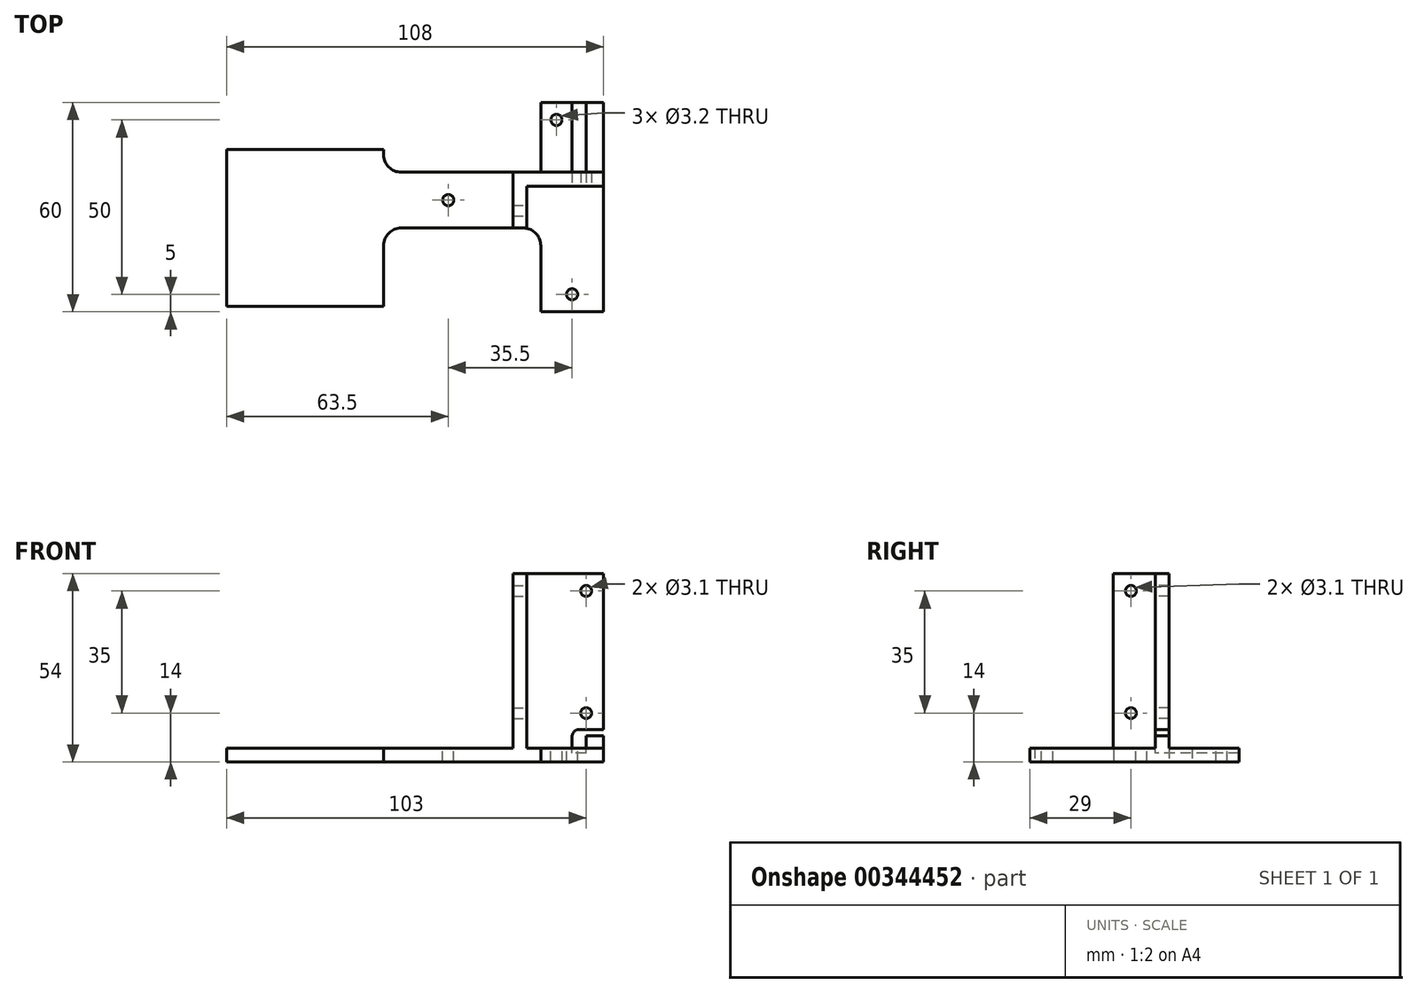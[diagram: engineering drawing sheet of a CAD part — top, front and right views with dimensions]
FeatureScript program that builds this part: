
annotation { "Feature Type Name" : "Feature", "Feature Type Description" : "" }
export const myFeature = defineFeature(function(context is Context, id is Id, definition is map)
    precondition{}
    {
        {
            var Q0;
            Q0=qCreatedBy(makeId("Top.planeOp"),FACE);
            var sketch = newSketch(context, id + "F0", { "sketchPlane" : qUnion([Q0])});
            skLineSegment(sketch, "E0", {"start": v(-54, 26.5) * mm, "end": v(-99, 26.5) * mm});
            skLineSegment(sketch, "E1", {"start": v(-99, 26.5) * mm, "end": v(-99, -18.5) * mm});
            skLineSegment(sketch, "E2", {"start": v(-99, -18.5) * mm, "end": v(-54, -18.5) * mm});
            skLineSegment(sketch, "E3", {"start": v(-54, -18.5) * mm, "end": v(-54, 4) * mm});
            skLineSegment(sketch, "E4", {"start": v(-54, 4) * mm, "end": v(-9, 4) * mm});
            skLineSegment(sketch, "E5", {"start": v(9, 20) * mm, "end": v(-54, 20) * mm});
            skLineSegment(sketch, "E6", {"start": v(-54, 20) * mm, "end": v(-54, 26.5) * mm});
            skLineSegment(sketch, "E7", {"start": v(-9, 4) * mm, "end": v(-9, -20) * mm});
            skLineSegment(sketch, "E8", {"start": v(-9, -20) * mm, "end": v(9, -20) * mm});
            skLineSegment(sketch, "E9", {"start": v(9, -20) * mm, "end": v(9, 20) * mm});
            skPoint(sketch, "E10", {"position": v(0, -20) * mm});
            skPoint(sketch, "E11", {"position": v(9, 0) * mm});
            skSolve(sketch);
        }
        {
            var Q0;
            Q0=makeQuery(id+"F0.imprint","IMPRINT",FACE,{"disambiguationData":[TD([[makeQuery(id+"F0.imprint","IMPRINT",EDGE,{"derivedFrom":sQuery(id+"F0.wireOp",EDGE,"E0")}),1.0]])]});
            extrude(context, id + "F1", {"entities" : qUnion([Q0]), "depth" : 4 * mm});
        }
        {
            var Q0;
            Q0=makeQuery(id+"F1.opExtrude","CAP_FACE",FACE,{"disambiguationData":[OSD([sQuery(id+"F0.wireOp",EDGE,"E0"),sQuery(id+"F0.wireOp",EDGE,"E1"),sQuery(id+"F0.wireOp",EDGE,"E2"),sQuery(id+"F0.wireOp",EDGE,"E3"),sQuery(id+"F0.wireOp",EDGE,"E4"),sQuery(id+"F0.wireOp",EDGE,"E5"),sQuery(id+"F0.wireOp",EDGE,"E6"),sQuery(id+"F0.wireOp",EDGE,"E7"),sQuery(id+"F0.wireOp",EDGE,"E8"),sQuery(id+"F0.wireOp",EDGE,"E9")])],"isStart":false});
            var sketch = newSketch(context, id + "F2", { "sketchPlane" : qUnion([Q0])});
            skLineSegment(sketch, "E12", {"start": v(-17, 4) * mm, "end": v(-17, 20) * mm});
            skPoint(sketch, "E12.endSnap0", {"position": v(-22.5, 20) * mm});
            skLineSegment(sketch, "E13", {"start": v(-17, 20) * mm, "end": v(9, 20) * mm});
            skLineSegment(sketch, "E14", {"start": v(9, 20) * mm, "end": v(9, 16) * mm});
            skLineSegment(sketch, "E15", {"start": v(9, 16) * mm, "end": v(-13, 16) * mm});
            skLineSegment(sketch, "E16", {"start": v(-13, 16) * mm, "end": v(-13, 4) * mm});
            skLineSegment(sketch, "E17", {"start": v(-13, 4) * mm, "end": v(-17, 4) * mm});
            skSolve(sketch);
        }
        {
            var Q0;
            Q0=makeQuery(id+"F2.imprint","IMPRINT",FACE,{"disambiguationData":[TD([[makeQuery(id+"F2.imprint","IMPRINT",EDGE,{"derivedFrom":sQuery(id+"F2.wireOp",EDGE,"E12")}),-1.0]])]});
            var Q1;
            Q1 = qSketchRegion(id + "F2", true);
            extrude(context, id + "F3", {"entities" : qUnion([Q0, Q1]), "operationType" : NewBodyOperationType.ADD, "depth" : 50 * mm});
        }
        {
            var Q0;
            Q0=makeQuery(id+"F3.opExtrude","SWEPT_FACE",FACE,{"disambiguationData":[OSD([sQuery(id+"F2.wireOp",EDGE,"E15")])]});
            var sketch = newSketch(context, id + "F4", { "sketchPlane" : qUnion([Q0])});
            skCircle(sketch, "E18", {"center": v(4, 49) * mm, "radius": 1.55 * mm});
            skCircle(sketch, "E19", {"center": v(4, 14) * mm, "radius": 1.55 * mm});
            skSolve(sketch);
        }
        {
            var Q0;
            Q0 = qSketchRegion(id + "F4", true);
            extrude(context, id + "F5", {"entities" : qUnion([Q0]), "operationType" : NewBodyOperationType.REMOVE, "endBound" : BoundingType.UP_TO_NEXT, "oppositeDirection" : true, "depth" : 25 * mm});
        }
        {
            var Q0;
            Q0=makeQuery(id+"F3.opExtrude","SWEPT_FACE",FACE,{"disambiguationData":[OSD([sQuery(id+"F2.wireOp",EDGE,"E16")])]});
            var sketch = newSketch(context, id + "F6", { "sketchPlane" : qUnion([Q0])});
            skCircle(sketch, "E20", {"center": v(9, 49) * mm, "radius": 1.55 * mm});
            skCircle(sketch, "E21", {"center": v(9, 14) * mm, "radius": 1.55 * mm});
            skSolve(sketch);
        }
        {
            var Q0;
            Q0 = qSketchRegion(id + "F6", true);
            extrude(context, id + "F7", {"entities" : qUnion([Q0]), "operationType" : NewBodyOperationType.REMOVE, "endBound" : BoundingType.UP_TO_NEXT, "oppositeDirection" : true, "depth" : 25 * mm});
        }
        {
            var Q0;
            Q0=makeQuery(id+"F3.opExtrude","SWEPT_FACE",FACE,{"disambiguationData":[OSD([sQuery(id+"F2.wireOp",EDGE,"E15")])]});
            var sketch = newSketch(context, id + "F8", { "sketchPlane" : qUnion([Q0])});
            skLineSegment(sketch, "E22", {"start": v(9, 9.3) * mm, "end": v(2, 9.3) * mm});
            skLineSegment(sketch, "E23", {"start": v(0, 7.3) * mm, "end": v(0, 4) * mm});
            skLineSegment(sketch, "E24", {"start": v(0, 4) * mm, "end": v(4, 4) * mm});
            skLineSegment(sketch, "E25", {"start": v(4, 4) * mm, "end": v(4, 7.5) * mm});
            skLineSegment(sketch, "E26", {"start": v(4, 7.5) * mm, "end": v(9, 7.5) * mm});
            skLineSegment(sketch, "E27", {"start": v(9, 7.5) * mm, "end": v(9, 9.3) * mm});
            skPoint(sketch, "E28.visualSharp", {"position": v(0, 9.3) * mm});
            skArc(sketch, "E28.filletArc", {"start": v(2, 9.3) * mm, "mid": v(0.59, 8.71) * mm, "end": v(0, 7.3) * mm});
            skSolve(sketch);
        }
        {
            var Q0;
            Q0 = qSketchRegion(id + "F8", true);
            extrude(context, id + "F9", {"entities" : qUnion([Q0]), "operationType" : NewBodyOperationType.REMOVE, "endBound" : BoundingType.UP_TO_NEXT, "oppositeDirection" : true, "depth" : 25 * mm});
        }
        {
            var Q0;
            Q0=makeQuery(id+"F3.boolean.opBoolean","MERGE",FACE,{"derivedFrom":[makeQuery(id+"F1.opExtrude","SWEPT_FACE",FACE,{"disambiguationData":[OSD([sQuery(id+"F0.wireOp",EDGE,"E5")])]}),makeQuery(id+"F3.opExtrude","SWEPT_FACE",FACE,{"disambiguationData":[OSD([sQuery(id+"F2.wireOp",EDGE,"E13")])]})]});
            var sketch = newSketch(context, id + "F10", { "sketchPlane" : qUnion([Q0])});
            skLineSegment(sketch, "E29.bottom", {"start": v(-9, 0) * mm, "end": v(9, 0) * mm});
            skLineSegment(sketch, "E29.top", {"start": v(-9, 4) * mm, "end": v(9, 4) * mm});
            skLineSegment(sketch, "E29.left", {"start": v(-9, 0) * mm, "end": v(-9, 4) * mm});
            skLineSegment(sketch, "E29.right", {"start": v(9, 0) * mm, "end": v(9, 4) * mm});
            skLineSegment(sketch, "E30.0.1", {"start": v(9, 0) * mm, "end": v(9, 4) * mm, "construction": true});
            skLineSegment(sketch, "E30.0.3", {"start": v(9, 4) * mm, "end": v(9, 0) * mm, "construction": true});
            skSolve(sketch);
        }
        {
            var Q0;
            Q0=makeQuery(id+"F10.imprint","IMPRINT",FACE,{"disambiguationData":[TD([[makeQuery(id+"F10.imprint","IMPRINT",EDGE,{"derivedFrom":sQuery(id+"F10.wireOp",EDGE,"E29.bottom")}),1.0]])]});
            extrude(context, id + "F11", {"entities" : qUnion([Q0]), "operationType" : NewBodyOperationType.ADD, "depth" : 20 * mm});
        }
        {
            var Q0;
            {var subQ0=sQuery(id+"F0.wireOp",EDGE,"E8");var subQ1=sQuery(id+"F0.wireOp",EDGE,"E7");var subQ2=sQuery(id+"F0.wireOp",EDGE,"E9");var subQ3=sQuery(id+"F0.wireOp",EDGE,"E4");Q0=makeQuery(id+"F11.boolean.opBoolean","MERGE",FACE,{"derivedFrom":[makeQuery(id+"F9.boolean.opBoolean","MERGE",FACE,{"derivedFrom":[makeQuery(id+"F3.boolean.opBoolean","SPLIT",FACE,{"disambiguationData":[TD([makeQuery(id+"F1.opExtrude","SWEPT_FACE",FACE,{"disambiguationData":[OSD([subQ1])]})])],"derivedFrom":makeQuery(id+"F1.opExtrude","CAP_FACE",FACE,{"disambiguationData":[OSD([sQuery(id+"F0.wireOp",EDGE,"E0"),sQuery(id+"F0.wireOp",EDGE,"E1"),sQuery(id+"F0.wireOp",EDGE,"E2"),sQuery(id+"F0.wireOp",EDGE,"E3"),subQ3,sQuery(id+"F0.wireOp",EDGE,"E5"),sQuery(id+"F0.wireOp",EDGE,"E6"),subQ1,subQ0,subQ2])],"isStart":false})}),makeQuery(id+"F9.opExtrude","SWEPT_FACE",FACE,{"disambiguationData":[OSD([sQuery(id+"F8.wireOp",EDGE,"E24")])]})]}),makeQuery(id+"F11.opExtrude","SWEPT_FACE",FACE,{"disambiguationData":[OSD([sQuery(id+"F10.wireOp",EDGE,"E29.top")])]})]});}
            var sketch = newSketch(context, id + "F12", { "sketchPlane" : qUnion([Q0])});
            skLineSegment(sketch, "E31.bottom", {"start": v(4, 16) * mm, "end": v(0, 16) * mm});
            skLineSegment(sketch, "E31.top", {"start": v(4, 40) * mm, "end": v(0, 40) * mm});
            skLineSegment(sketch, "E31.left", {"start": v(4, 16) * mm, "end": v(4, 40) * mm});
            skLineSegment(sketch, "E31.right", {"start": v(0, 16) * mm, "end": v(0, 40) * mm});
            skSolve(sketch);
        }
        {
            var Q0;
            {var subQ8=sQuery(id+"F12.wireOp",EDGE,"E31.bottom");Q0=makeQuery(id+"F12.imprint","IMPRINT",FACE,{"disambiguationData":[TD([[makeQuery(id+"F12.imprint","IMPRINT",EDGE,{"derivedFrom":subQ8}),-1.0]])]});}
            extrude(context, id + "F13", {"entities" : qUnion([Q0]), "operationType" : NewBodyOperationType.REMOVE, "oppositeDirection" : true, "depth" : 1.5 * mm});
        }
        {
            var Q0;
            {var subQ0=makeQuery(id+"F3.opExtrude","SWEPT_FACE",FACE,{"disambiguationData":[OSD([sQuery(id+"F2.wireOp",EDGE,"E15")])]});var subQ1=sQuery(id+"F0.wireOp",EDGE,"E7");var subQ2=makeQuery(id+"F1.opExtrude","SWEPT_FACE",FACE,{"disambiguationData":[OSD([subQ1])]});var subQ3=makeQuery(id+"F3.opExtrude","SWEPT_FACE",FACE,{"disambiguationData":[OSD([sQuery(id+"F2.wireOp",EDGE,"E17")])]});var subQ4=sQuery(id+"F0.wireOp",EDGE,"E9");var subQ5=makeQuery(id+"F1.opExtrude","SWEPT_FACE",FACE,{"disambiguationData":[OSD([subQ4])]});var subQ6=makeQuery(id+"F3.opExtrude","SWEPT_FACE",FACE,{"disambiguationData":[OSD([sQuery(id+"F2.wireOp",EDGE,"E16")])]});var subQ7=sQuery(id+"F0.wireOp",EDGE,"E8");var subQ8=makeQuery(id+"F1.opExtrude","SWEPT_FACE",FACE,{"disambiguationData":[OSD([subQ7])]});var subQ9=makeQuery(id+"F3.opExtrude","SWEPT_FACE",FACE,{"disambiguationData":[OSD([sQuery(id+"F2.wireOp",EDGE,"E14")])]});var subQ10=sQuery(id+"F0.wireOp",EDGE,"E4");var subQ11=makeQuery(id+"F1.opExtrude","SWEPT_FACE",FACE,{"disambiguationData":[OSD([subQ10])]});Q0=makeQuery(id+"F13.boolean.opBoolean","SPLIT",FACE,{"disambiguationData":[TD([subQ11,subQ2,subQ8,subQ5,subQ9,subQ0,subQ6,subQ3,makeQuery(id+"F9.boolean.opBoolean","COPY",FACE,{"derivedFrom":makeQuery(id+"F9.opExtrude","SWEPT_FACE",FACE,{"disambiguationData":[OSD([sQuery(id+"F8.wireOp",EDGE,"E23")])]})}),makeQuery(id+"F9.boolean.opBoolean","COPY",FACE,{"derivedFrom":makeQuery(id+"F9.opExtrude","SWEPT_FACE",FACE,{"disambiguationData":[OSD([sQuery(id+"F8.wireOp",EDGE,"E25")])]})}),makeQuery(id+"F11.opExtrude","SWEPT_FACE",FACE,{"disambiguationData":[OSD([sQuery(id+"F10.wireOp",EDGE,"E29.left")])]}),makeQuery(id+"F13.opExtrude","SWEPT_FACE",FACE,{"disambiguationData":[OSD([sQuery(id+"F12.wireOp",EDGE,"E31.bottom")])]}),makeQuery(id+"F13.opExtrude","SWEPT_FACE",FACE,{"disambiguationData":[OSD([sQuery(id+"F12.wireOp",EDGE,"E31.left")])]}),makeQuery(id+"F13.opExtrude","SWEPT_FACE",FACE,{"disambiguationData":[OSD([sQuery(id+"F12.wireOp",EDGE,"E31.right")])]})])],"derivedFrom":makeQuery(id+"F11.boolean.opBoolean","MERGE",FACE,{"derivedFrom":[makeQuery(id+"F9.boolean.opBoolean","MERGE",FACE,{"derivedFrom":[makeQuery(id+"F3.boolean.opBoolean","SPLIT",FACE,{"disambiguationData":[TD([subQ2])],"derivedFrom":makeQuery(id+"F1.opExtrude","CAP_FACE",FACE,{"disambiguationData":[OSD([sQuery(id+"F0.wireOp",EDGE,"E0"),sQuery(id+"F0.wireOp",EDGE,"E1"),sQuery(id+"F0.wireOp",EDGE,"E2"),sQuery(id+"F0.wireOp",EDGE,"E3"),subQ10,sQuery(id+"F0.wireOp",EDGE,"E5"),sQuery(id+"F0.wireOp",EDGE,"E6"),subQ1,subQ7,subQ4])],"isStart":false})}),makeQuery(id+"F9.opExtrude","SWEPT_FACE",FACE,{"disambiguationData":[OSD([sQuery(id+"F8.wireOp",EDGE,"E24")])]})]}),makeQuery(id+"F11.opExtrude","SWEPT_FACE",FACE,{"disambiguationData":[OSD([sQuery(id+"F10.wireOp",EDGE,"E29.top")])]})]})});}
            var sketch = newSketch(context, id + "F14", { "sketchPlane" : qUnion([Q0])});
            skCircle(sketch, "E32", {"center": v(0, -15) * mm, "radius": 1.6 * mm});
            skPoint(sketch, "E32.centerSnap0", {"position": v(0, -20) * mm});
            skSolve(sketch);
        }
        {
            var Q0;
            Q0=makeQuery(id+"F14.imprint","IMPRINT",FACE,{"disambiguationData":[TD([[makeQuery(id+"F14.imprint","IMPRINT",EDGE,{"derivedFrom":sQuery(id+"F14.wireOp",EDGE,"E32")}),1.0]])]});
            extrude(context, id + "F15", {"entities" : qUnion([Q0]), "operationType" : NewBodyOperationType.REMOVE, "endBound" : BoundingType.UP_TO_NEXT, "oppositeDirection" : true, "depth" : 25 * mm});
        }
        {
            var Q0;
            {var subQ0=sQuery(id+"F0.wireOp",EDGE,"E2");var subQ1=sQuery(id+"F0.wireOp",EDGE,"E1");var subQ2=sQuery(id+"F0.wireOp",EDGE,"E3");var subQ3=sQuery(id+"F0.wireOp",EDGE,"E0");var subQ4=sQuery(id+"F0.wireOp",EDGE,"E4");var subQ5=sQuery(id+"F0.wireOp",EDGE,"E5");var subQ6=sQuery(id+"F0.wireOp",EDGE,"E6");Q0=makeQuery(id+"F3.boolean.opBoolean","SPLIT",FACE,{"disambiguationData":[TD([makeQuery(id+"F1.opExtrude","SWEPT_FACE",FACE,{"disambiguationData":[OSD([subQ3])]})])],"derivedFrom":makeQuery(id+"F1.opExtrude","CAP_FACE",FACE,{"disambiguationData":[OSD([subQ3,subQ1,subQ0,subQ2,subQ4,subQ5,subQ6,sQuery(id+"F0.wireOp",EDGE,"E7"),sQuery(id+"F0.wireOp",EDGE,"E8"),sQuery(id+"F0.wireOp",EDGE,"E9")])],"isStart":false})});}
            var sketch = newSketch(context, id + "F16", { "sketchPlane" : qUnion([Q0])});
            skCircle(sketch, "E33", {"center": v(-35.5, 12) * mm, "radius": 1.6 * mm});
            skPoint(sketch, "E33.centerSnap0", {"position": v(-35.5, 20) * mm});
            skPoint(sketch, "E34", {"position": v(-17, 12) * mm});
            skSolve(sketch);
        }
        {
            var Q0;
            Q0 = qSketchRegion(id + "F16", true);
            extrude(context, id + "F17", {"entities" : qUnion([Q0]), "operationType" : NewBodyOperationType.REMOVE, "endBound" : BoundingType.UP_TO_NEXT, "oppositeDirection" : true, "depth" : 25 * mm});
        }
        {
            var Q0;
            {var subQ0=sQuery(id+"F10.wireOp",EDGE,"E29.right");var subQ1=sQuery(id+"F10.wireOp",EDGE,"E29.top");var subQ2=sQuery(id+"F0.wireOp",EDGE,"E5");var subQ3=sQuery(id+"F0.wireOp",EDGE,"E8");var subQ4=sQuery(id+"F0.wireOp",EDGE,"E7");var subQ5=sQuery(id+"F0.wireOp",EDGE,"E9");var subQ6=sQuery(id+"F0.wireOp",EDGE,"E4");Q0=makeQuery(id+"F13.boolean.opBoolean","SPLIT",FACE,{"disambiguationData":[TD([makeQuery(id+"F1.opExtrude","SWEPT_FACE",FACE,{"disambiguationData":[OSD([subQ2])]}),makeQuery(id+"F3.opExtrude","SWEPT_FACE",FACE,{"disambiguationData":[OSD([sQuery(id+"F2.wireOp",EDGE,"E13")])]}),makeQuery(id+"F9.boolean.opBoolean","COPY",FACE,{"derivedFrom":makeQuery(id+"F9.opExtrude","SWEPT_FACE",FACE,{"disambiguationData":[OSD([sQuery(id+"F8.wireOp",EDGE,"E23")])]})}),makeQuery(id+"F11.opExtrude","CAP_FACE",FACE,{"disambiguationData":[OSD([sQuery(id+"F10.wireOp",EDGE,"E29.bottom"),subQ1,sQuery(id+"F10.wireOp",EDGE,"E29.left"),subQ0])],"isStart":false}),makeQuery(id+"F11.opExtrude","SWEPT_FACE",FACE,{"disambiguationData":[OSD([subQ0])]}),makeQuery(id+"F13.opExtrude","SWEPT_FACE",FACE,{"disambiguationData":[OSD([sQuery(id+"F12.wireOp",EDGE,"E31.right")])]})])],"derivedFrom":makeQuery(id+"F11.boolean.opBoolean","MERGE",FACE,{"derivedFrom":[makeQuery(id+"F9.boolean.opBoolean","MERGE",FACE,{"derivedFrom":[makeQuery(id+"F3.boolean.opBoolean","SPLIT",FACE,{"disambiguationData":[TD([makeQuery(id+"F1.opExtrude","SWEPT_FACE",FACE,{"disambiguationData":[OSD([subQ4])]})])],"derivedFrom":makeQuery(id+"F1.opExtrude","CAP_FACE",FACE,{"disambiguationData":[OSD([sQuery(id+"F0.wireOp",EDGE,"E0"),sQuery(id+"F0.wireOp",EDGE,"E1"),sQuery(id+"F0.wireOp",EDGE,"E2"),sQuery(id+"F0.wireOp",EDGE,"E3"),subQ6,subQ2,sQuery(id+"F0.wireOp",EDGE,"E6"),subQ4,subQ3,subQ5])],"isStart":false})}),makeQuery(id+"F9.opExtrude","SWEPT_FACE",FACE,{"disambiguationData":[OSD([sQuery(id+"F8.wireOp",EDGE,"E24")])]})]}),makeQuery(id+"F11.opExtrude","SWEPT_FACE",FACE,{"disambiguationData":[OSD([subQ1])]})]})});}
            var sketch = newSketch(context, id + "F18", { "sketchPlane" : qUnion([Q0])});
            skCircle(sketch, "E35", {"center": v(-4.5, 35) * mm, "radius": 1.6 * mm});
            skPoint(sketch, "E35.centerSnap0", {"position": v(-4.5, 40) * mm});
            skSolve(sketch);
        }
        {
            var Q0;
            Q0 = qSketchRegion(id + "F18", true);
            extrude(context, id + "F19", {"entities" : qUnion([Q0]), "operationType" : NewBodyOperationType.REMOVE, "endBound" : BoundingType.UP_TO_NEXT, "oppositeDirection" : true, "depth" : 25 * mm});
        }
        {
            var Q0;
            Q0=makeQuery(id+"F3.opExtrude","CAP_EDGE",EDGE,{"disambiguationData":[OSD([sQuery(id+"F2.wireOp",EDGE,"E12")])],"isStart":true});
            var Q1;
            {var subQ1=sQuery(id+"F10.wireOp",EDGE,"E29.top");Q1=makeQuery(id+"F11.boolean.opBoolean","SPLIT",EDGE,{"disambiguationData":[TD([makeQuery(id+"F9.boolean.opBoolean","COPY",FACE,{"derivedFrom":makeQuery(id+"F9.opExtrude","SWEPT_FACE",FACE,{"disambiguationData":[OSD([sQuery(id+"F8.wireOp",EDGE,"E23")])]})})])],"derivedFrom":makeQuery(id+"F11.opExtrude","CAP_EDGE",EDGE,{"disambiguationData":[OSD([subQ1])],"isStart":true})});}
            var Q2;
            {var subQ0=sQuery(id+"F0.wireOp",EDGE,"E9");var subQ2=sQuery(id+"F10.wireOp",EDGE,"E29.top");Q2=makeQuery(id+"F11.boolean.opBoolean","SPLIT",EDGE,{"disambiguationData":[TD([makeQuery(id+"F1.opExtrude","SWEPT_FACE",FACE,{"disambiguationData":[OSD([subQ0])]})])],"derivedFrom":makeQuery(id+"F11.opExtrude","CAP_EDGE",EDGE,{"disambiguationData":[OSD([subQ2])],"isStart":true})});}
            var Q3;
            Q3=makeQuery(id+"F11.opExtrude","CAP_EDGE",EDGE,{"disambiguationData":[OSD([sQuery(id+"F10.wireOp",EDGE,"E29.right")])],"isStart":true});
            var Q4;
            Q4=makeQuery(id+"F1.opExtrude","SWEPT_EDGE",EDGE,{"disambiguationData":[OSD([sQuery(id+"F0.wireOp",EDGE,"E4"),sQuery(id+"F0.wireOp",EDGE,"E7")])]});
            var Q5;
            Q5=makeQuery(id+"F1.opExtrude","SWEPT_EDGE",EDGE,{"disambiguationData":[OSD([sQuery(id+"F0.wireOp",EDGE,"E3"),sQuery(id+"F0.wireOp",EDGE,"E4")])]});
            var Q6;
            Q6=makeQuery(id+"F1.opExtrude","SWEPT_EDGE",EDGE,{"disambiguationData":[OSD([sQuery(id+"F0.wireOp",EDGE,"E5"),sQuery(id+"F0.wireOp",EDGE,"E6")])]});
            fillet(context, id + "F20", {"entities" : qUnion([Q0, Q1, Q2, Q3, Q4, Q5, Q6]), "radius" : 5 * mm, "tangentPropagation" : true, "allowEdgeOverflow" : false});
        }
    });
